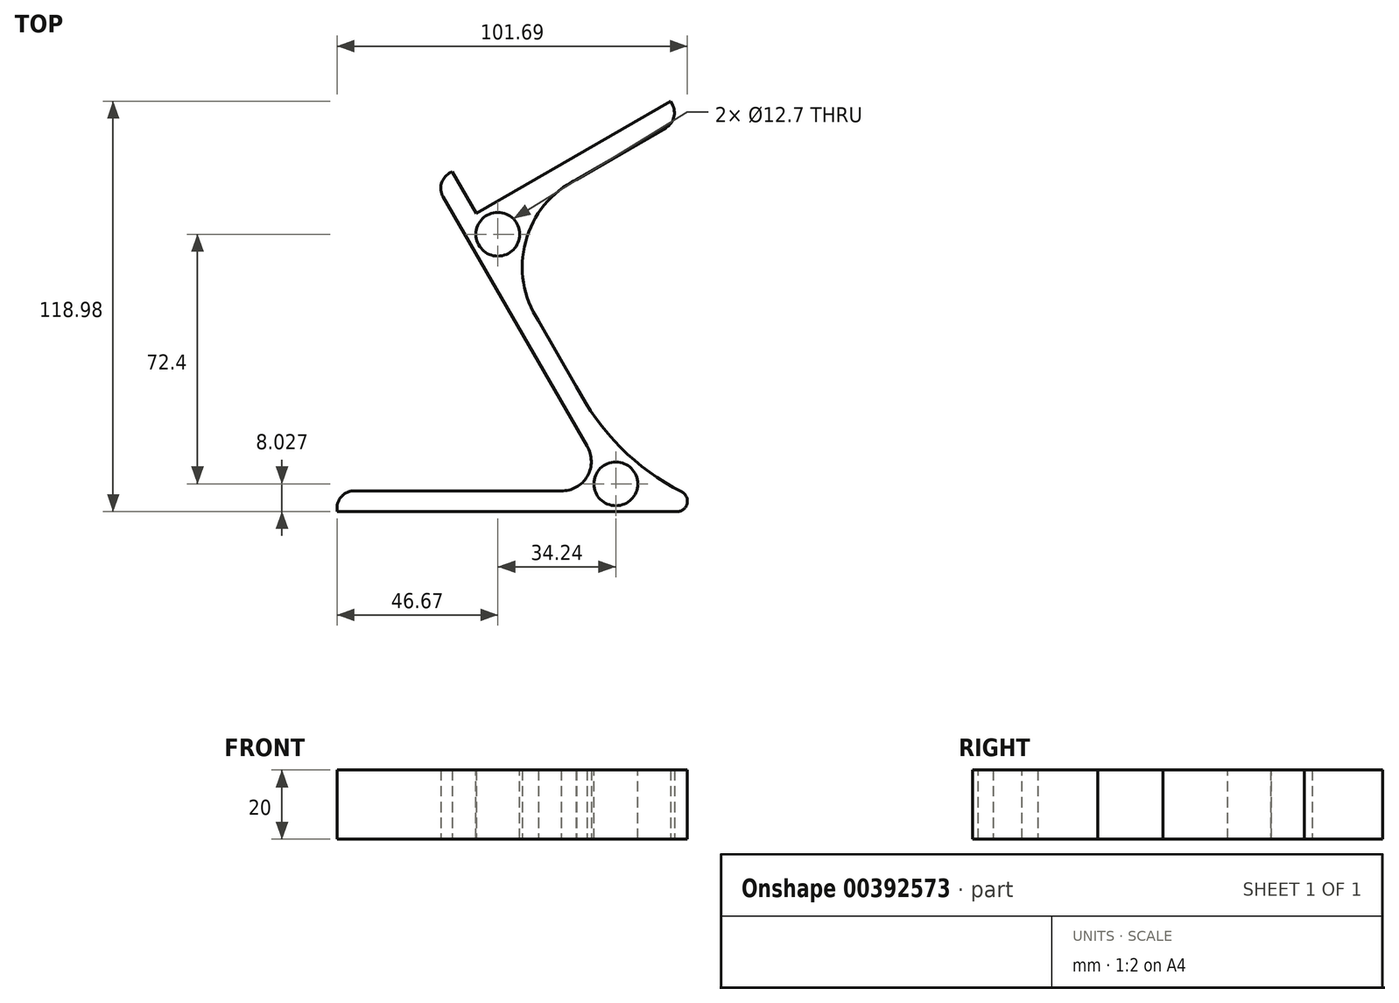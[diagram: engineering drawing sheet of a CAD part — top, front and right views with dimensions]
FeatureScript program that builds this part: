
annotation { "Feature Type Name" : "Feature", "Feature Type Description" : "" }
export const myFeature = defineFeature(function(context is Context, id is Id, definition is map)
    precondition{}
    {
        {
            var Q0;
            Q0=qCreatedBy(makeId("Top.planeOp"),FACE);
            var sketch = newSketch(context, id + "F0", { "sketchPlane" : qUnion([Q0])});
            skLineSegment(sketch, "E0", {"start": v(-90.4, -30.33) * mm, "end": v(0, -30.33) * mm});
            skPoint(sketch, "E1.endSnap0", {"position": v(-45.2, -30.33) * mm});
            skLineSegment(sketch, "E2", {"start": v(-53.7, 50.67) * mm, "end": v(-10.4, -24.33) * mm});
            skLineSegment(sketch, "E3", {"start": v(-10.4, -24.33) * mm, "end": v(-90.4, -24.33) * mm});
            skLineSegment(sketch, "E4", {"start": v(-90.4, -24.33) * mm, "end": v(-90.4, -30.33) * mm});
            skLineSegment(sketch, "E5", {"start": v(-53.7, 50.67) * mm, "end": v(-62.13, 65.28) * mm});
            skLineSegment(sketch, "E6", {"start": v(-62.13, 65.28) * mm, "end": v(-56.93, 68.28) * mm});
            skLineSegment(sketch, "E7", {"start": v(-56.93, 68.28) * mm, "end": v(-49.93, 56.15) * mm});
            skLineSegment(sketch, "E8", {"start": v(-49.93, 56.15) * mm, "end": v(6.36, 88.65) * mm});
            skLineSegment(sketch, "E9", {"start": v(-46.93, 50.96) * mm, "end": v(9.36, 83.46) * mm});
            skLineSegment(sketch, "E10", {"start": v(9.36, 83.46) * mm, "end": v(6.36, 88.65) * mm});
            skPoint(sketch, "E11", {"position": v(-20.95, 65.96) * mm});
            skPoint(sketch, "E12", {"position": v(-31.93, 24.98) * mm});
            skPoint(sketch, "E13", {"position": v(-10.4, -24.33) * mm});
            skPoint(sketch, "E14", {"position": v(-27.9, 5.98) * mm});
            skPoint(sketch, "E15", {"position": v(-45.4, -24.33) * mm});
            skArc(sketch, "E16", {"start": v(-20.95, 65.96) * mm, "mid": v(-35.68, 47.94) * mm, "end": v(-31.93, 24.98) * mm});
            skLineSegment(sketch, "E17", {"start": v(0, -30.33) * mm, "end": v(25, -30.33) * mm});
            skPoint(sketch, "E18", {"position": v(-20.96, 5.98) * mm});
            skArc(sketch, "E19", {"start": v(-20.96, 5.98) * mm, "mid": v(-1.96, -17.2) * mm, "end": v(25, -30.33) * mm});
            skLineSegment(sketch, "E20", {"start": v(-31.93, 24.98) * mm, "end": v(-20.96, 5.98) * mm});
            skPoint(sketch, "E21", {"position": v(-17.9, -11.34) * mm});
            skPoint(sketch, "E22", {"position": v(-25.4, -24.33) * mm});
            skArc(sketch, "E23", {"start": v(-25.4, -24.33) * mm, "mid": v(-17.75, -20.08) * mm, "end": v(-17.9, -11.34) * mm});
            skSolve(sketch);
        }
        {
            var Q0;
            Q0=makeQuery(id+"F0.imprint","IMPRINT",FACE,{"disambiguationData":[TD([[makeQuery(id+"F0.imprint","IMPRINT",EDGE,{"derivedFrom":sQuery(id+"F0.wireOp",EDGE,"E0")}),1.0]])]});
            var Q1;
            {var subQ0=sQuery(id+"F0.wireOp",EDGE,"E9");var subQ1=sQuery(id+"F0.wireOp",EDGE,"l1TTxDQ8-E2n2-j4fF-Accn-xfxl1YIgJ8KU");var subQ2=makeQuery(id+"F0.imprint","INTERSECT",VERTEX,{"derivedFrom":[subQ1,subQ0]});Q1=makeQuery(id+"F0.imprint","IMPRINT",FACE,{"disambiguationData":[TD([[makeQuery(id+"F0.imprint","IMPRINT",EDGE,{"disambiguationData":[TD([[subQ2,1.0]])],"derivedFrom":subQ1}),-1.0]])]});}
            var Q2;
            {var subQ0=sQuery(id+"F0.wireOp",EDGE,"E3");var subQ1=sQuery(id+"F0.wireOp",EDGE,"E2");var subQ2=makeQuery(id+"F0.imprint","INTERSECT",VERTEX,{"derivedFrom":[subQ1,subQ0]});Q2=makeQuery(id+"F0.imprint","IMPRINT",FACE,{"disambiguationData":[TD([[makeQuery(id+"F0.imprint","IMPRINT",EDGE,{"disambiguationData":[TD([[subQ2,1.0]])],"derivedFrom":subQ1}),-1.0]])]});}
            extrude(context, id + "F1", {"entities" : qUnion([Q0, Q1, Q2]), "depth" : 20 * mm});
        }
        {
            var Q0;
            Q0=makeQuery(id+"F1.opExtrude","SWEPT_EDGE",EDGE,{"disambiguationData":[OSD([sQuery(id+"F0.wireOp",EDGE,"E3"),sQuery(id+"F0.wireOp",EDGE,"E4")])]});
            var Q1;
            Q1=makeQuery(id+"F1.opExtrude","SWEPT_EDGE",EDGE,{"disambiguationData":[OSD([sQuery(id+"F0.wireOp",EDGE,"E5"),sQuery(id+"F0.wireOp",EDGE,"E6")])]});
            var Q2;
            Q2=makeQuery(id+"F1.opExtrude","SWEPT_EDGE",EDGE,{"disambiguationData":[OSD([sQuery(id+"F0.wireOp",EDGE,"E9"),sQuery(id+"F0.wireOp",EDGE,"E10")])]});
            fillet(context, id + "F2", {"entities" : qUnion([Q0, Q1, Q2]), "radius" : 5 * mm, "tangentPropagation" : true, "allowEdgeOverflow" : false});
        }
        {
            var Q0;
            Q0=makeQuery(id+"F1.opExtrude","CAP_FACE",FACE,{"disambiguationData":[OSD([sQuery(id+"F0.wireOp",EDGE,"E0"),sQuery(id+"F0.wireOp",EDGE,"E2"),sQuery(id+"F0.wireOp",EDGE,"E3"),sQuery(id+"F0.wireOp",EDGE,"E4"),sQuery(id+"F0.wireOp",EDGE,"l1TTxDQ8-E2n2-j4fF-Accn-xfxl1YIgJ8KU"),sQuery(id+"F0.wireOp",EDGE,"E5"),sQuery(id+"F0.wireOp",EDGE,"E6"),sQuery(id+"F0.wireOp",EDGE,"E7"),sQuery(id+"F0.wireOp",EDGE,"E8"),sQuery(id+"F0.wireOp",EDGE,"E9"),sQuery(id+"F0.wireOp",EDGE,"E10"),sQuery(id+"F0.wireOp",EDGE,"h9jw4Zwp-2nLZ-kFdP-WlIx-Qu4CgEQZul9Y"),sQuery(id+"F0.wireOp",EDGE,"E16")])],"isStart":false});
            var sketch = newSketch(context, id + "F3", { "sketchPlane" : qUnion([Q0])});
            skCircle(sketch, "E24", {"center": v(-43.72, 50.1) * mm, "radius": 6.35 * mm});
            skCircle(sketch, "E25", {"center": v(-9.48, -22.3) * mm, "radius": 6.35 * mm});
            skSolve(sketch);
        }
        {
            var Q0;
            Q0=makeQuery(id+"F3.imprint","IMPRINT",FACE,{"disambiguationData":[TD([[makeQuery(id+"F3.imprint","IMPRINT",EDGE,{"derivedFrom":sQuery(id+"F3.wireOp",EDGE,"E24")}),1.0]])]});
            var Q1;
            Q1=makeQuery(id+"F3.imprint","IMPRINT",FACE,{"disambiguationData":[TD([[makeQuery(id+"F3.imprint","IMPRINT",EDGE,{"derivedFrom":sQuery(id+"F3.wireOp",EDGE,"rwDHOaS7-9pr0-xwyl-AIln-TERcqXOqVT6l")}),1.0]])]});
            var Q2;
            Q2=makeQuery(id+"F3.imprint","IMPRINT",FACE,{"disambiguationData":[TD([[makeQuery(id+"F3.imprint","IMPRINT",EDGE,{"derivedFrom":sQuery(id+"F3.wireOp",EDGE,"E25")}),1.0]])]});
            extrude(context, id + "F4", {"entities" : qUnion([Q0, Q1, Q2]), "operationType" : NewBodyOperationType.REMOVE, "oppositeDirection" : true, "depth" : 25 * mm});
        }
        {
            var Q0;
            Q0=makeQuery(id+"F1.opExtrude","SWEPT_EDGE",EDGE,{"disambiguationData":[OSD([sQuery(id+"F0.wireOp",EDGE,"E17"),sQuery(id+"F0.wireOp",EDGE,"E19")])]});
            fillet(context, id + "F5", {"entities" : qUnion([Q0]), "radius" : 3 * mm, "tangentPropagation" : true, "allowEdgeOverflow" : false});
        }
    });
